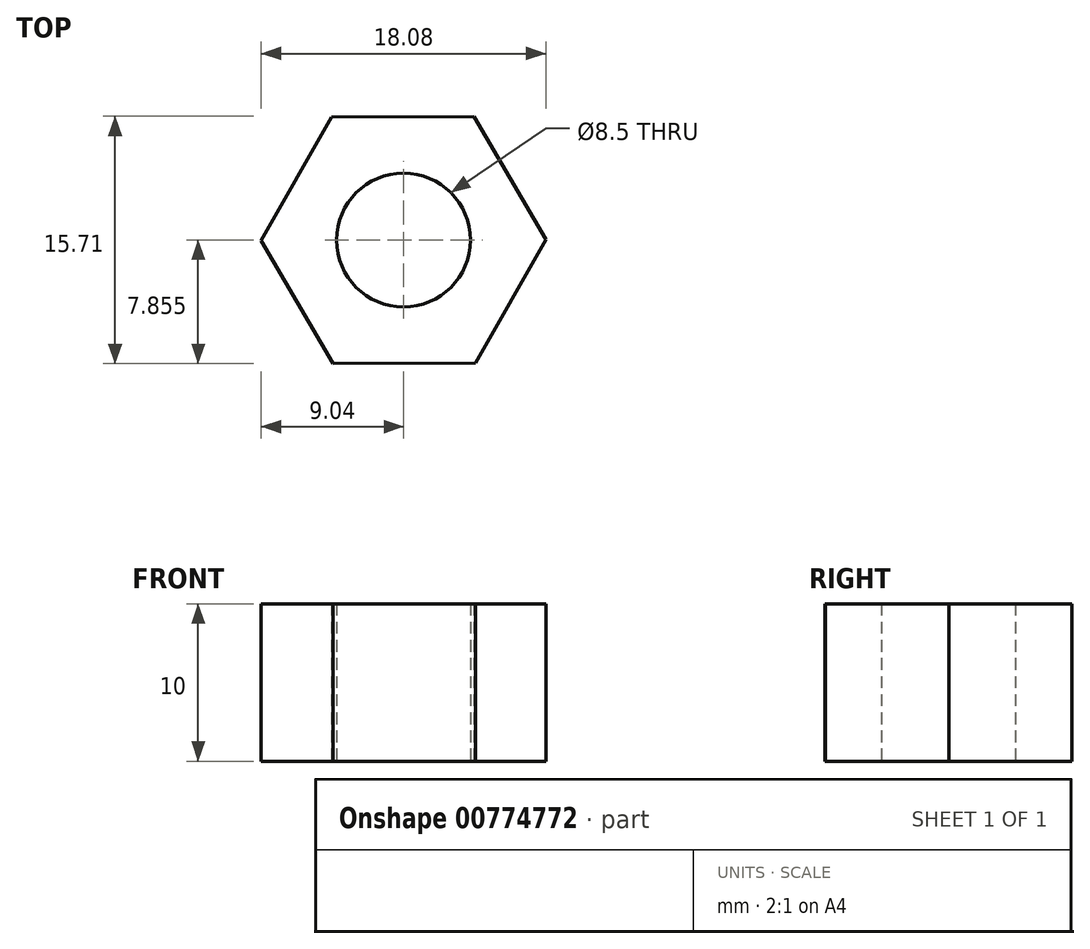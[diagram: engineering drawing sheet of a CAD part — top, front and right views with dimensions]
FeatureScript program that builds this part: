
annotation { "Feature Type Name" : "Feature", "Feature Type Description" : "" }
export const myFeature = defineFeature(function(context is Context, id is Id, definition is map)
    precondition{}
    {
        {
            var Q0;
            Q0=qCreatedBy(makeId("Top.planeOp"),FACE);
            var sketch = newSketch(context, id + "F0", { "sketchPlane" : qUnion([Q0])});
            skCircle(sketch, "E0", {"center": v(-18.77, 12.25) * mm, "radius": 4.25 * mm});
            skCircle(sketch, "E1.cCircle", {"center": v(-18.77, 12.25) * mm, "radius": 7.83 * mm, "construction": true});
            skLineSegment(sketch, "E1.0", {"start": v(-14.28, 20.1) * mm, "end": v(-9.73, 12.3) * mm});
            skLineSegment(sketch, "E1.1", {"start": v(-9.73, 12.3) * mm, "end": v(-14.21, 4.44) * mm});
            skLineSegment(sketch, "E1.2", {"start": v(-14.21, 4.44) * mm, "end": v(-23.25, 4.4) * mm});
            skLineSegment(sketch, "E1.3", {"start": v(-23.25, 4.4) * mm, "end": v(-27.81, 12.21) * mm});
            skLineSegment(sketch, "E1.4", {"start": v(-27.81, 12.21) * mm, "end": v(-23.33, 20.06) * mm});
            skLineSegment(sketch, "E1.5", {"start": v(-23.33, 20.06) * mm, "end": v(-14.28, 20.1) * mm});
            skPoint(sketch, "E1.0.midPoint", {"position": v(-12, 16.2) * mm});
            skSolve(sketch);
        }
        {
            var Q0;
            Q0=makeQuery(id+"F0.imprint","IMPRINT",FACE,{"disambiguationData":[TD([[makeQuery(id+"F0.imprint","IMPRINT",EDGE,{"derivedFrom":sQuery(id+"F0.wireOp",EDGE,"E0")}),-1.0]])]});
            extrude(context, id + "F1", {"entities" : qUnion([Q0]), "depth" : 10 * mm, "offsetDistance" : 25.4 * mm});
        }
    });
